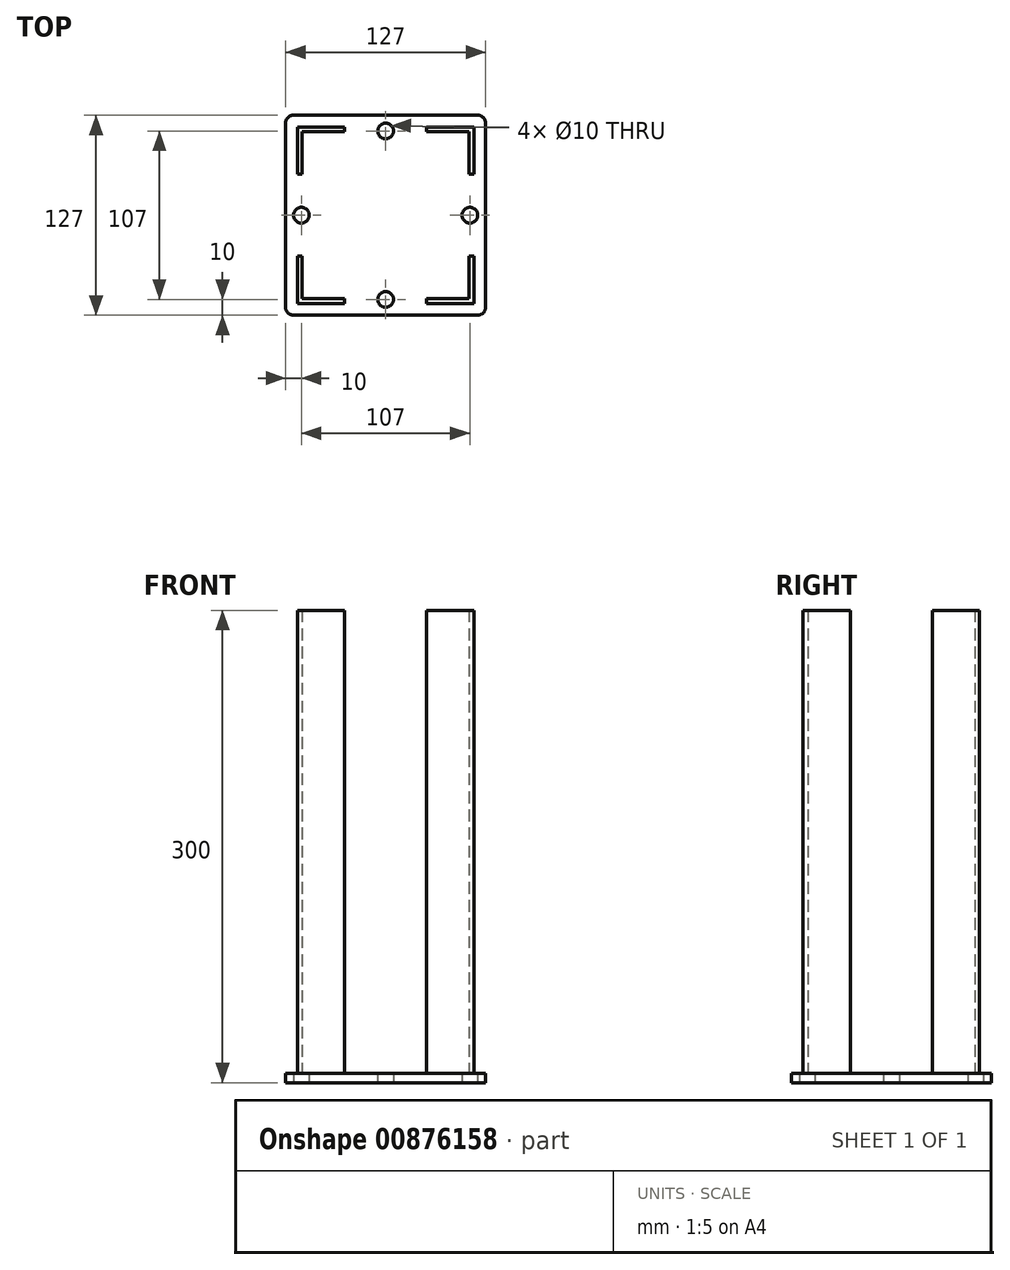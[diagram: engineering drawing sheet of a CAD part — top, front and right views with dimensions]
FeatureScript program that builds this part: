
annotation { "Feature Type Name" : "Feature", "Feature Type Description" : "" }
export const myFeature = defineFeature(function(context is Context, id is Id, definition is map)
    precondition{}
    {
        {
            var Q0;
            Q0=qCreatedBy(makeId("Top.planeOp"),FACE);
            var sketch = newSketch(context, id + "F0", { "sketchPlane" : qUnion([Q0])});
            skPoint(sketch, "E0.middle", {"position": v(0, 0) * mm});
            skLineSegment(sketch, "E1", {"start": v(-56, 56) * mm, "end": v(-56, 26) * mm});
            skLineSegment(sketch, "E2", {"start": v(-56, 56) * mm, "end": v(-26, 56) * mm});
            skLineSegment(sketch, "E3", {"start": v(26, 56) * mm, "end": v(56, 56) * mm});
            skLineSegment(sketch, "E4", {"start": v(56, 56) * mm, "end": v(56, 26) * mm});
            skLineSegment(sketch, "E5", {"start": v(56, -26) * mm, "end": v(56, -56) * mm});
            skLineSegment(sketch, "E6", {"start": v(56, -56) * mm, "end": v(26, -56) * mm});
            skLineSegment(sketch, "E7", {"start": v(-56, -26) * mm, "end": v(-56, -56) * mm});
            skLineSegment(sketch, "E8", {"start": v(-56, -56) * mm, "end": v(-26, -56) * mm});
            skLineSegment(sketch, "E9.0", {"start": v(-53, -53) * mm, "end": v(-26, -53) * mm});
            skLineSegment(sketch, "E9.1", {"start": v(-53, -26) * mm, "end": v(-53, -53) * mm});
            skLineSegment(sketch, "E10", {"start": v(-56, -26) * mm, "end": v(-53, -26) * mm});
            skLineSegment(sketch, "E11", {"start": v(-26, -53) * mm, "end": v(-26, -56) * mm});
            skPoint(sketch, "E12.start.orphan", {"position": v(56, -26) * mm});
            skLineSegment(sketch, "E13.0", {"start": v(53, -53) * mm, "end": v(26, -53) * mm});
            skLineSegment(sketch, "E13.1", {"start": v(53, -26) * mm, "end": v(53, -53) * mm});
            skLineSegment(sketch, "E14.0", {"start": v(53, 53) * mm, "end": v(53, 26) * mm});
            skLineSegment(sketch, "E14.1", {"start": v(26, 53) * mm, "end": v(53, 53) * mm});
            skLineSegment(sketch, "E15.0", {"start": v(-53, 53) * mm, "end": v(-26, 53) * mm});
            skLineSegment(sketch, "E15.1", {"start": v(-53, 53) * mm, "end": v(-53, 26) * mm});
            skLineSegment(sketch, "E16", {"start": v(53, -26) * mm, "end": v(56, -26) * mm});
            skLineSegment(sketch, "E17", {"start": v(26, -53) * mm, "end": v(26, -56) * mm});
            skLineSegment(sketch, "E18", {"start": v(56, 26) * mm, "end": v(53, 26) * mm});
            skLineSegment(sketch, "E19", {"start": v(26, 56) * mm, "end": v(26, 53) * mm});
            skLineSegment(sketch, "E20", {"start": v(-26, 56) * mm, "end": v(-26, 53) * mm});
            skLineSegment(sketch, "E21", {"start": v(-56, 26) * mm, "end": v(-53, 26) * mm});
            skPoint(sketch, "E22.orphan", {"position": v(-56, 41) * mm});
            skPoint(sketch, "E23.start.orphan", {"position": v(-56, -41) * mm});
            skPoint(sketch, "E24.start.orphan", {"position": v(56, -41) * mm});
            skLineSegment(sketch, "E25.bottom", {"start": v(58.5, -63.5) * mm, "end": v(-58.5, -63.5) * mm});
            skLineSegment(sketch, "E25.top", {"start": v(58.5, 63.5) * mm, "end": v(-58.5, 63.5) * mm});
            skLineSegment(sketch, "E25.left", {"start": v(63.5, -58.5) * mm, "end": v(63.5, 58.5) * mm});
            skLineSegment(sketch, "E25.right", {"start": v(-63.5, -58.5) * mm, "end": v(-63.5, 58.5) * mm});
            skPoint(sketch, "E26.visualSharp", {"position": v(-63.5, 63.5) * mm});
            skArc(sketch, "E26.filletArc", {"start": v(-58.5, 63.5) * mm, "mid": v(-62.04, 62.04) * mm, "end": v(-63.5, 58.5) * mm});
            skPoint(sketch, "E27.visualSharp", {"position": v(63.5, 63.5) * mm});
            skArc(sketch, "E27.filletArc", {"start": v(63.5, 58.5) * mm, "mid": v(62.04, 62.04) * mm, "end": v(58.5, 63.5) * mm});
            skPoint(sketch, "E28.visualSharp", {"position": v(63.5, -63.5) * mm});
            skArc(sketch, "E28.filletArc", {"start": v(58.5, -63.5) * mm, "mid": v(62.04, -62.04) * mm, "end": v(63.5, -58.5) * mm});
            skPoint(sketch, "E29.visualSharp", {"position": v(-63.5, -63.5) * mm});
            skArc(sketch, "E29.filletArc", {"start": v(-63.5, -58.5) * mm, "mid": v(-62.04, -62.04) * mm, "end": v(-58.5, -63.5) * mm});
            skLineSegment(sketch, "E30", {"start": v(0, 74.64) * mm, "end": v(0, -79.13) * mm});
            skPoint(sketch, "E30.endSnap0", {"position": v(0, 63.5) * mm});
            skLineSegment(sketch, "E31", {"start": v(-73, 0) * mm, "end": v(98.55, 0) * mm});
            skCircle(sketch, "E32", {"center": v(0, 53.5) * mm, "radius": 5 * mm});
            skCircle(sketch, "E33", {"center": v(53.5, 0) * mm, "radius": 5 * mm});
            skCircle(sketch, "E34", {"center": v(0, -53.5) * mm, "radius": 5 * mm});
            skCircle(sketch, "E35", {"center": v(-53.5, 0) * mm, "radius": 5 * mm});
            skSolve(sketch);
        }
        {
            var Q0;
            Q0=qSketchRegion(id+"F0",true);
            extrude(context, id + "F1", {"entities" : qUnion([Q0]), "depth" : 6 * mm});
        }
        {
            var Q0;
            Q0=makeQuery(id+"F0.imprint","IMPRINT",FACE,{"disambiguationData":[TD([[makeQuery(id+"F0.imprint","IMPRINT",EDGE,{"derivedFrom":sQuery(id+"F0.wireOp",EDGE,"E5")}),-1.0]])]});
            var Q1;
            Q1=makeQuery(id+"F0.imprint","IMPRINT",FACE,{"disambiguationData":[TD([[makeQuery(id+"F0.imprint","IMPRINT",EDGE,{"derivedFrom":sQuery(id+"F0.wireOp",EDGE,"E3")}),-1.0]])]});
            var Q2;
            Q2=makeQuery(id+"F0.imprint","IMPRINT",FACE,{"disambiguationData":[TD([[makeQuery(id+"F0.imprint","IMPRINT",EDGE,{"derivedFrom":sQuery(id+"F0.wireOp",EDGE,"E1")}),1.0]])]});
            var Q3;
            Q3=makeQuery(id+"F0.imprint","IMPRINT",FACE,{"disambiguationData":[TD([[makeQuery(id+"F0.imprint","IMPRINT",EDGE,{"derivedFrom":sQuery(id+"F0.wireOp",EDGE,"E7")}),1.0]])]});
            extrude(context, id + "F2", {"entities" : qUnion([Q0, Q1, Q2, Q3]), "operationType" : NewBodyOperationType.ADD, "depth" : 300 * mm, "offsetDistance" : 25 * mm});
        }
    });
